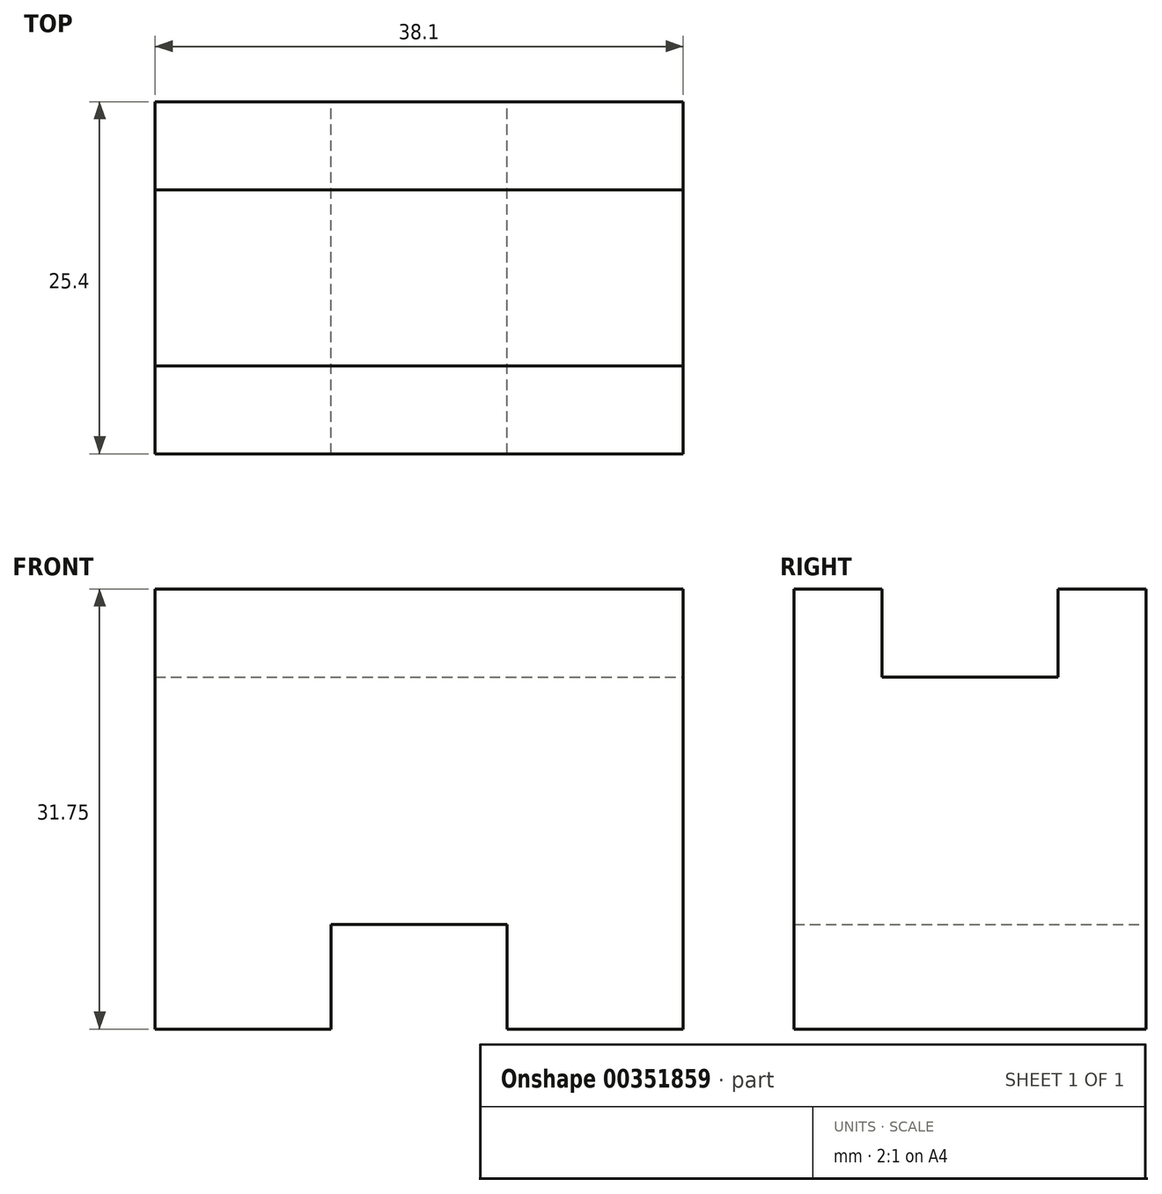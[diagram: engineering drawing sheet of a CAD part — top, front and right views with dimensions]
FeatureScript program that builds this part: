
annotation { "Feature Type Name" : "Feature", "Feature Type Description" : "" }
export const myFeature = defineFeature(function(context is Context, id is Id, definition is map)
    precondition{}
    {
        {
            var Q0;
            Q0=qCreatedBy(makeId("Front.planeOp"),FACE);
            var sketch = newSketch(context, id + "F0", { "sketchPlane" : qUnion([Q0])});
            skLineSegment(sketch, "E0", {"start": v(0, 0) * mm, "end": v(12.7, 0) * mm});
            skLineSegment(sketch, "E1", {"start": v(12.7, 0) * mm, "end": v(12.7, 7.53) * mm});
            skLineSegment(sketch, "E2", {"start": v(12.7, 7.53) * mm, "end": v(25.4, 7.53) * mm});
            skLineSegment(sketch, "E3", {"start": v(25.4, 7.53) * mm, "end": v(25.4, 0) * mm});
            skLineSegment(sketch, "E4", {"start": v(25.4, 0) * mm, "end": v(38.1, 0) * mm});
            skLineSegment(sketch, "E5", {"start": v(38.1, 0) * mm, "end": v(38.1, 31.75) * mm});
            skLineSegment(sketch, "E6", {"start": v(38.1, 31.75) * mm, "end": v(0, 31.75) * mm});
            skLineSegment(sketch, "E7", {"start": v(0, 31.75) * mm, "end": v(0, 0) * mm});
            skSolve(sketch);
        }
        {
            var Q0;
            Q0=makeQuery(id+"F0.imprint","IMPRINT",FACE,{"disambiguationData":[TD([[makeQuery(id+"F0.imprint","IMPRINT",EDGE,{"derivedFrom":sQuery(id+"F0.wireOp",EDGE,"E0")}),1.0]])]});
            extrude(context, id + "F1", {"entities" : qUnion([Q0]), "depth" : 25.4 * mm});
        }
        {
            var Q0;
            Q0=makeQuery(id+"F1.opExtrude","SWEPT_FACE",FACE,{"disambiguationData":[OSD([sQuery(id+"F0.wireOp",EDGE,"E5")])]});
            var sketch = newSketch(context, id + "F2", { "sketchPlane" : qUnion([Q0])});
            skLineSegment(sketch, "E8", {"start": v(-19.05, 31.75) * mm, "end": v(-19.05, 25.4) * mm});
            skLineSegment(sketch, "E9", {"start": v(-19.05, 25.4) * mm, "end": v(-6.35, 25.4) * mm});
            skLineSegment(sketch, "E10", {"start": v(-6.35, 25.4) * mm, "end": v(-6.35, 31.75) * mm});
            skSolve(sketch);
        }
        {
            var Q0;
            {var subQ0=sQuery(id+"F2.wireOp",EDGE,"E8");Q0=makeQuery(id+"F2.imprint","IMPRINT",FACE,{"disambiguationData":[TD([[makeQuery(id+"F2.imprint","IMPRINT",EDGE,{"derivedFrom":subQ0}),1.0]])]});}
            extrude(context, id + "F3", {"entities" : qUnion([Q0]), "operationType" : NewBodyOperationType.REMOVE, "oppositeDirection" : true, "depth" : 49.53 * mm});
        }
    });
